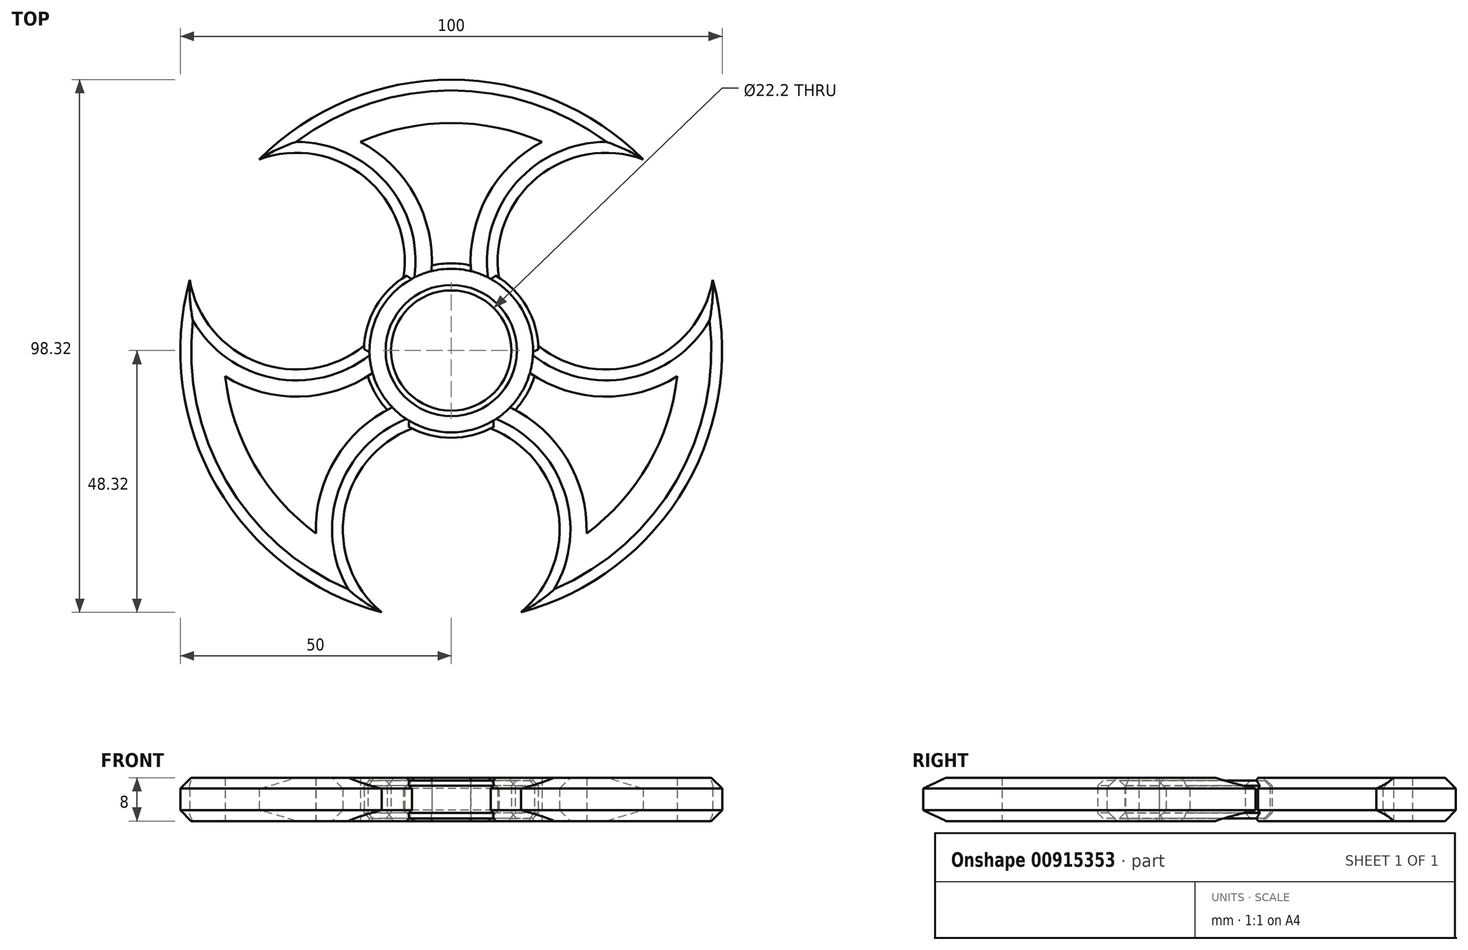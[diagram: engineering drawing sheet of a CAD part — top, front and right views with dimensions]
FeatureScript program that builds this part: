
annotation { "Feature Type Name" : "Feature", "Feature Type Description" : "" }
export const myFeature = defineFeature(function(context is Context, id is Id, definition is map)
    precondition{}
    {
        {
            var Q0;
            Q0=qCreatedBy(makeId("Top.planeOp"),FACE);
            var sketch = newSketch(context, id + "F0", { "sketchPlane" : qUnion([Q0])});
            skCircle(sketch, "E0", {"center": v(0, 0) * mm, "radius": 11.1 * mm});
            skCircle(sketch, "E1", {"center": v(0, 0) * mm, "radius": 16.1 * mm});
            skSolve(sketch);
        }
        {
            var Q0;
            Q0=makeQuery(id+"F0.imprint","IMPRINT",FACE,{"disambiguationData":[TD([[makeQuery(id+"F0.imprint","IMPRINT",EDGE,{"derivedFrom":sQuery(id+"F0.wireOp",EDGE,"E0")}),-1.0]])]});
            extrude(context, id + "F1", {"entities" : qUnion([Q0]), "endBound" : BoundingType.SYMMETRIC, "depth" : 7 * mm, "offsetDistance" : 25 * mm});
        }
        {
            var Q0;
            Q0=makeQuery(id+"F1.opExtrude","CAP_FACE",FACE,{"disambiguationData":[OSD([sQuery(id+"F0.wireOp",EDGE,"E0"),sQuery(id+"F0.wireOp",EDGE,"E1")])],"isStart":false});
            var Q1;
            Q1=makeQuery(id+"F1.opExtrude","CAP_FACE",FACE,{"disambiguationData":[OSD([sQuery(id+"F0.wireOp",EDGE,"E0"),sQuery(id+"F0.wireOp",EDGE,"E1")])],"isStart":true});
            chamfer(context, id + "F2", {"entities" : qUnion([Q0, Q1]), "width" : 1 * mm, "tangentPropagation" : true});
        }
        {
            var Q0;
            Q0=qCreatedBy(makeId("Top.planeOp"),FACE);
            var sketch = newSketch(context, id + "F3", { "sketchPlane" : qUnion([Q0])});
            skArc(sketch, "E2", {"start": v(-48.27, 13.02) * mm, "mid": v(-43.3, -25) * mm, "end": v(-12.86, -48.32) * mm});
            skArc(sketch, "E3", {"start": v(12.86, -48.32) * mm, "mid": v(0, -13) * mm, "end": v(-12.86, -48.32) * mm});
            skArc(sketch, "E4.1.0", {"start": v(35.42, 35.3) * mm, "mid": v(11.26, 6.5) * mm, "end": v(48.27, 13.02) * mm});
            skArc(sketch, "E4.2.0", {"start": v(-48.27, 13.02) * mm, "mid": v(-11.26, 6.5) * mm, "end": v(-35.42, 35.3) * mm});
            skArc(sketch, "E5.trimOffspring", {"start": v(35.42, 35.3) * mm, "mid": v(0, 50) * mm, "end": v(-35.42, 35.3) * mm});
            skArc(sketch, "E6.trimOffspring", {"start": v(12.86, -48.32) * mm, "mid": v(43.3, -25) * mm, "end": v(48.27, 13.02) * mm});
            skCircle(sketch, "E7", {"center": v(0, 0) * mm, "radius": 12.5 * mm});
            skArc(sketch, "E8.0", {"start": v(16.74, 38.52) * mm, "mid": v(0, 42) * mm, "end": v(-16.74, 38.52) * mm});
            skArc(sketch, "E9.trimOffspring", {"start": v(-4.02, 11.84) * mm, "mid": v(-6.01, 27.26) * mm, "end": v(-16.74, 38.52) * mm});
            skArc(sketch, "E10.MirrorCS", {"start": v(4.02, 11.84) * mm, "mid": v(6.01, 27.26) * mm, "end": v(16.74, 38.52) * mm});
            skArc(sketch, "E11.1.0", {"start": v(-41.73, -4.76) * mm, "mid": v(-36.37, -21) * mm, "end": v(-24.99, -33.76) * mm});
            skArc(sketch, "E11.1.1", {"start": v(-12.26, -2.44) * mm, "mid": v(-26.61, -8.42) * mm, "end": v(-41.73, -4.76) * mm});
            skArc(sketch, "E11.1.2", {"start": v(-8.24, -9.4) * mm, "mid": v(-20.6, -18.84) * mm, "end": v(-24.99, -33.76) * mm});
            skArc(sketch, "E11.2.0", {"start": v(24.99, -33.76) * mm, "mid": v(36.37, -21) * mm, "end": v(41.73, -4.76) * mm});
            skArc(sketch, "E11.2.1", {"start": v(8.24, -9.4) * mm, "mid": v(20.6, -18.84) * mm, "end": v(24.99, -33.76) * mm});
            skArc(sketch, "E11.2.2", {"start": v(12.26, -2.44) * mm, "mid": v(26.61, -8.42) * mm, "end": v(41.73, -4.76) * mm});
            skSolve(sketch);
        }
        {
            var Q0;
            Q0=makeQuery(id+"F3.imprint","IMPRINT",FACE,{"disambiguationData":[TD([[makeQuery(id+"F3.imprint","IMPRINT",EDGE,{"derivedFrom":sQuery(id+"F3.wireOp",EDGE,"E2")}),1.0]])]});
            extrude(context, id + "F4", {"entities" : qUnion([Q0]), "operationType" : NewBodyOperationType.ADD, "endBound" : BoundingType.SYMMETRIC, "depth" : 8 * mm, "offsetDistance" : 25 * mm});
        }
        {
            var Q0;
            {var subQ3=sQuery(id+"F3.wireOp",EDGE,"E9.trimOffspring");var subQ7=sQuery(id+"F0.wireOp",EDGE,"E0");var subQ8=sQuery(id+"F0.wireOp",EDGE,"E1");Q0=makeQuery(id+"F4.boolean.opBoolean","SPLIT",FACE,{"disambiguationData":[TD([makeQuery(id+"F4.opExtrude","SWEPT_FACE",FACE,{"disambiguationData":[OSD([subQ3])]})])],"derivedFrom":makeQuery(id+"F1.opExtrude","CAP_FACE",FACE,{"disambiguationData":[OSD([subQ7,subQ8])],"isStart":false})});}
            var sketch = newSketch(context, id + "F5", { "sketchPlane" : qUnion([Q0])});
            skCircle(sketch, "E12", {"center": v(0, 0) * mm, "radius": 15.1 * mm});
            skSolve(sketch);
        }
        {
            var Q0;
            Q0 = qSketchRegion(id + "F5", true);
            var Q1;
            Q1=sQuery(id+"F5.wireOp",EDGE,"E12");
            extrude(context, id + "F6", {"entities" : qUnion([Q0]), "operationType" : NewBodyOperationType.REMOVE, "surfaceEntities" : qUnion([Q1]), "depth" : 25 * mm, "offsetDistance" : 25 * mm});
        }
        {
            var Q0;
            {var subQ6=sQuery(id+"F0.wireOp",EDGE,"E0");var subQ7=sQuery(id+"F3.wireOp",EDGE,"E9.trimOffspring");var subQ8=sQuery(id+"F0.wireOp",EDGE,"E1");Q0=makeQuery(id+"F4.boolean.opBoolean","SPLIT",FACE,{"disambiguationData":[TD([makeQuery(id+"F4.opExtrude","SWEPT_FACE",FACE,{"disambiguationData":[OSD([subQ7])]})])],"derivedFrom":makeQuery(id+"F1.opExtrude","CAP_FACE",FACE,{"disambiguationData":[OSD([subQ6,subQ8])],"isStart":true})});}
            var sketch = newSketch(context, id + "F7", { "sketchPlane" : qUnion([Q0])});
            skCircle(sketch, "E13", {"center": v(0, 0) * mm, "radius": 15.1 * mm});
            skSolve(sketch);
        }
        {
            var Q0;
            Q0 = qSketchRegion(id + "F7", true);
            extrude(context, id + "F8", {"entities" : qUnion([Q0]), "operationType" : NewBodyOperationType.REMOVE, "depth" : 25 * mm, "offsetDistance" : 25 * mm});
        }
        {
            var Q0;
            Q0=makeQuery(id+"F4.opExtrude","CAP_EDGE",EDGE,{"disambiguationData":[OSD([sQuery(id+"F3.wireOp",EDGE,"E6.trimOffspring")])],"isStart":false});
            var Q1;
            {var subQ0=sQuery(id+"F3.wireOp",EDGE,"E6.trimOffspring");var subQ1=sQuery(id+"F3.wireOp",EDGE,"E3");Q1=makeQuery(id+"F6.boolean.opBoolean","SPLIT",EDGE,{"disambiguationData":[TD([makeQuery(id+"F4.opExtrude","SWEPT_FACE",FACE,{"disambiguationData":[OSD([subQ0])]})])],"derivedFrom":makeQuery(id+"F4.opExtrude","CAP_EDGE",EDGE,{"disambiguationData":[OSD([subQ1])],"isStart":false})});}
            var Q2;
            {var subQ0=sQuery(id+"F3.wireOp",EDGE,"E6.trimOffspring");var subQ1=sQuery(id+"F3.wireOp",EDGE,"E4.1.0");Q2=makeQuery(id+"F6.boolean.opBoolean","SPLIT",EDGE,{"disambiguationData":[TD([makeQuery(id+"F4.opExtrude","SWEPT_FACE",FACE,{"disambiguationData":[OSD([subQ0])]})])],"derivedFrom":makeQuery(id+"F4.opExtrude","CAP_EDGE",EDGE,{"disambiguationData":[OSD([subQ1])],"isStart":false})});}
            var Q3;
            {var subQ0=sQuery(id+"F3.wireOp",EDGE,"E5.trimOffspring");var subQ1=sQuery(id+"F3.wireOp",EDGE,"E4.1.0");Q3=makeQuery(id+"F6.boolean.opBoolean","SPLIT",EDGE,{"disambiguationData":[TD([makeQuery(id+"F4.opExtrude","SWEPT_FACE",FACE,{"disambiguationData":[OSD([subQ0])]})])],"derivedFrom":makeQuery(id+"F4.opExtrude","CAP_EDGE",EDGE,{"disambiguationData":[OSD([subQ1])],"isStart":false})});}
            var Q4;
            Q4=makeQuery(id+"F4.opExtrude","CAP_EDGE",EDGE,{"disambiguationData":[OSD([sQuery(id+"F3.wireOp",EDGE,"E5.trimOffspring")])],"isStart":false});
            var Q5;
            {var subQ0=sQuery(id+"F3.wireOp",EDGE,"E5.trimOffspring");var subQ1=sQuery(id+"F3.wireOp",EDGE,"E4.2.0");Q5=makeQuery(id+"F6.boolean.opBoolean","SPLIT",EDGE,{"disambiguationData":[TD([makeQuery(id+"F4.opExtrude","SWEPT_FACE",FACE,{"disambiguationData":[OSD([subQ0])]})])],"derivedFrom":makeQuery(id+"F4.opExtrude","CAP_EDGE",EDGE,{"disambiguationData":[OSD([subQ1])],"isStart":false})});}
            var Q6;
            {var subQ0=sQuery(id+"F3.wireOp",EDGE,"E2");var subQ1=sQuery(id+"F3.wireOp",EDGE,"E4.2.0");Q6=makeQuery(id+"F6.boolean.opBoolean","SPLIT",EDGE,{"disambiguationData":[TD([makeQuery(id+"F4.opExtrude","SWEPT_FACE",FACE,{"disambiguationData":[OSD([subQ0])]})])],"derivedFrom":makeQuery(id+"F4.opExtrude","CAP_EDGE",EDGE,{"disambiguationData":[OSD([subQ1])],"isStart":false})});}
            var Q7;
            Q7=makeQuery(id+"F4.opExtrude","CAP_EDGE",EDGE,{"disambiguationData":[OSD([sQuery(id+"F3.wireOp",EDGE,"E2")])],"isStart":false});
            var Q8;
            {var subQ0=sQuery(id+"F3.wireOp",EDGE,"E2");var subQ1=sQuery(id+"F3.wireOp",EDGE,"E3");Q8=makeQuery(id+"F6.boolean.opBoolean","SPLIT",EDGE,{"disambiguationData":[TD([makeQuery(id+"F4.opExtrude","SWEPT_FACE",FACE,{"disambiguationData":[OSD([subQ0])]})])],"derivedFrom":makeQuery(id+"F4.opExtrude","CAP_EDGE",EDGE,{"disambiguationData":[OSD([subQ1])],"isStart":false})});}
            var Q9;
            Q9=makeQuery(id+"F4.opExtrude","CAP_EDGE",EDGE,{"disambiguationData":[OSD([sQuery(id+"F3.wireOp",EDGE,"E6.trimOffspring")])],"isStart":true});
            var Q10;
            {var subQ0=sQuery(id+"F3.wireOp",EDGE,"E6.trimOffspring");var subQ1=sQuery(id+"F3.wireOp",EDGE,"E4.1.0");Q10=makeQuery(id+"F8.boolean.opBoolean","SPLIT",EDGE,{"disambiguationData":[TD([makeQuery(id+"F4.opExtrude","SWEPT_FACE",FACE,{"disambiguationData":[OSD([subQ0])]})])],"derivedFrom":makeQuery(id+"F4.opExtrude","CAP_EDGE",EDGE,{"disambiguationData":[OSD([subQ1])],"isStart":true})});}
            var Q11;
            {var subQ0=sQuery(id+"F3.wireOp",EDGE,"E6.trimOffspring");var subQ1=sQuery(id+"F3.wireOp",EDGE,"E3");Q11=makeQuery(id+"F8.boolean.opBoolean","SPLIT",EDGE,{"disambiguationData":[TD([makeQuery(id+"F4.opExtrude","SWEPT_FACE",FACE,{"disambiguationData":[OSD([subQ0])]})])],"derivedFrom":makeQuery(id+"F4.opExtrude","CAP_EDGE",EDGE,{"disambiguationData":[OSD([subQ1])],"isStart":true})});}
            var Q12;
            {var subQ0=sQuery(id+"F3.wireOp",EDGE,"E2");var subQ1=sQuery(id+"F3.wireOp",EDGE,"E3");Q12=makeQuery(id+"F8.boolean.opBoolean","SPLIT",EDGE,{"disambiguationData":[TD([makeQuery(id+"F4.opExtrude","SWEPT_FACE",FACE,{"disambiguationData":[OSD([subQ0])]})])],"derivedFrom":makeQuery(id+"F4.opExtrude","CAP_EDGE",EDGE,{"disambiguationData":[OSD([subQ1])],"isStart":true})});}
            var Q13;
            Q13=makeQuery(id+"F4.opExtrude","CAP_EDGE",EDGE,{"disambiguationData":[OSD([sQuery(id+"F3.wireOp",EDGE,"E2")])],"isStart":true});
            var Q14;
            {var subQ0=sQuery(id+"F3.wireOp",EDGE,"E2");var subQ1=sQuery(id+"F3.wireOp",EDGE,"E4.2.0");Q14=makeQuery(id+"F8.boolean.opBoolean","SPLIT",EDGE,{"disambiguationData":[TD([makeQuery(id+"F4.opExtrude","SWEPT_FACE",FACE,{"disambiguationData":[OSD([subQ0])]})])],"derivedFrom":makeQuery(id+"F4.opExtrude","CAP_EDGE",EDGE,{"disambiguationData":[OSD([subQ1])],"isStart":true})});}
            var Q15;
            {var subQ0=sQuery(id+"F3.wireOp",EDGE,"E5.trimOffspring");var subQ1=sQuery(id+"F3.wireOp",EDGE,"E4.2.0");Q15=makeQuery(id+"F8.boolean.opBoolean","SPLIT",EDGE,{"disambiguationData":[TD([makeQuery(id+"F4.opExtrude","SWEPT_FACE",FACE,{"disambiguationData":[OSD([subQ0])]})])],"derivedFrom":makeQuery(id+"F4.opExtrude","CAP_EDGE",EDGE,{"disambiguationData":[OSD([subQ1])],"isStart":true})});}
            var Q16;
            Q16=makeQuery(id+"F4.opExtrude","CAP_EDGE",EDGE,{"disambiguationData":[OSD([sQuery(id+"F3.wireOp",EDGE,"E5.trimOffspring")])],"isStart":true});
            var Q17;
            {var subQ0=sQuery(id+"F3.wireOp",EDGE,"E5.trimOffspring");var subQ1=sQuery(id+"F3.wireOp",EDGE,"E4.1.0");Q17=makeQuery(id+"F8.boolean.opBoolean","SPLIT",EDGE,{"disambiguationData":[TD([makeQuery(id+"F4.opExtrude","SWEPT_FACE",FACE,{"disambiguationData":[OSD([subQ0])]})])],"derivedFrom":makeQuery(id+"F4.opExtrude","CAP_EDGE",EDGE,{"disambiguationData":[OSD([subQ1])],"isStart":true})});}
            chamfer(context, id + "F9", {"entities" : qUnion([Q0, Q1, Q2, Q3, Q4, Q5, Q6, Q7, Q8, Q9, Q10, Q11, Q12, Q13, Q14, Q15, Q16, Q17]), "width" : 2 * mm, "tangentPropagation" : true});
        }
    });
